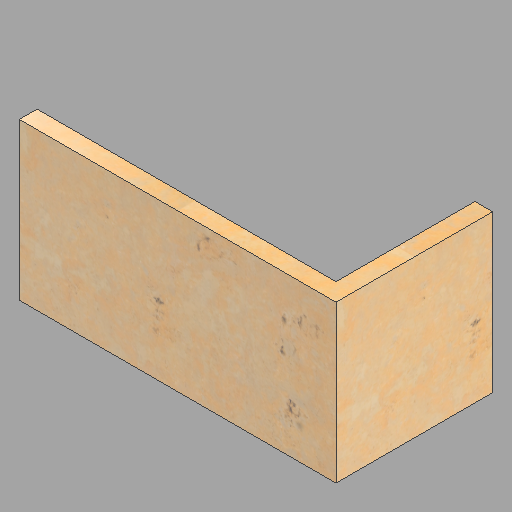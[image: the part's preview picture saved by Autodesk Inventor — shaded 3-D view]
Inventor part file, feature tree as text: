
AUTODESK INVENTOR PART (.ipt)
format: ipt  version: 2023 (Build 270158030, 158C)  size: 284,672 bytes
history: native  units: in
note: dims shown in document units (in); Inventor stores cm internally (conversion verified against a paired STEP export)
features: extrude x1, sketch x1
ambient origin geometry x8: Origin, YZ Plane, XZ Plane, XY Plane, X Axis, Y Axis, Z Axis, Center Point
bodies: Solid1 (feature_tree)
feature tree (2):
  extrude  "Extrusion1"  Depth=2.0in
  sketch  "Sketch1"  dims[d0=35.625in d1=2.0in d2=17.625in d3=2.0in d4=17.625in d5=0.0in]
